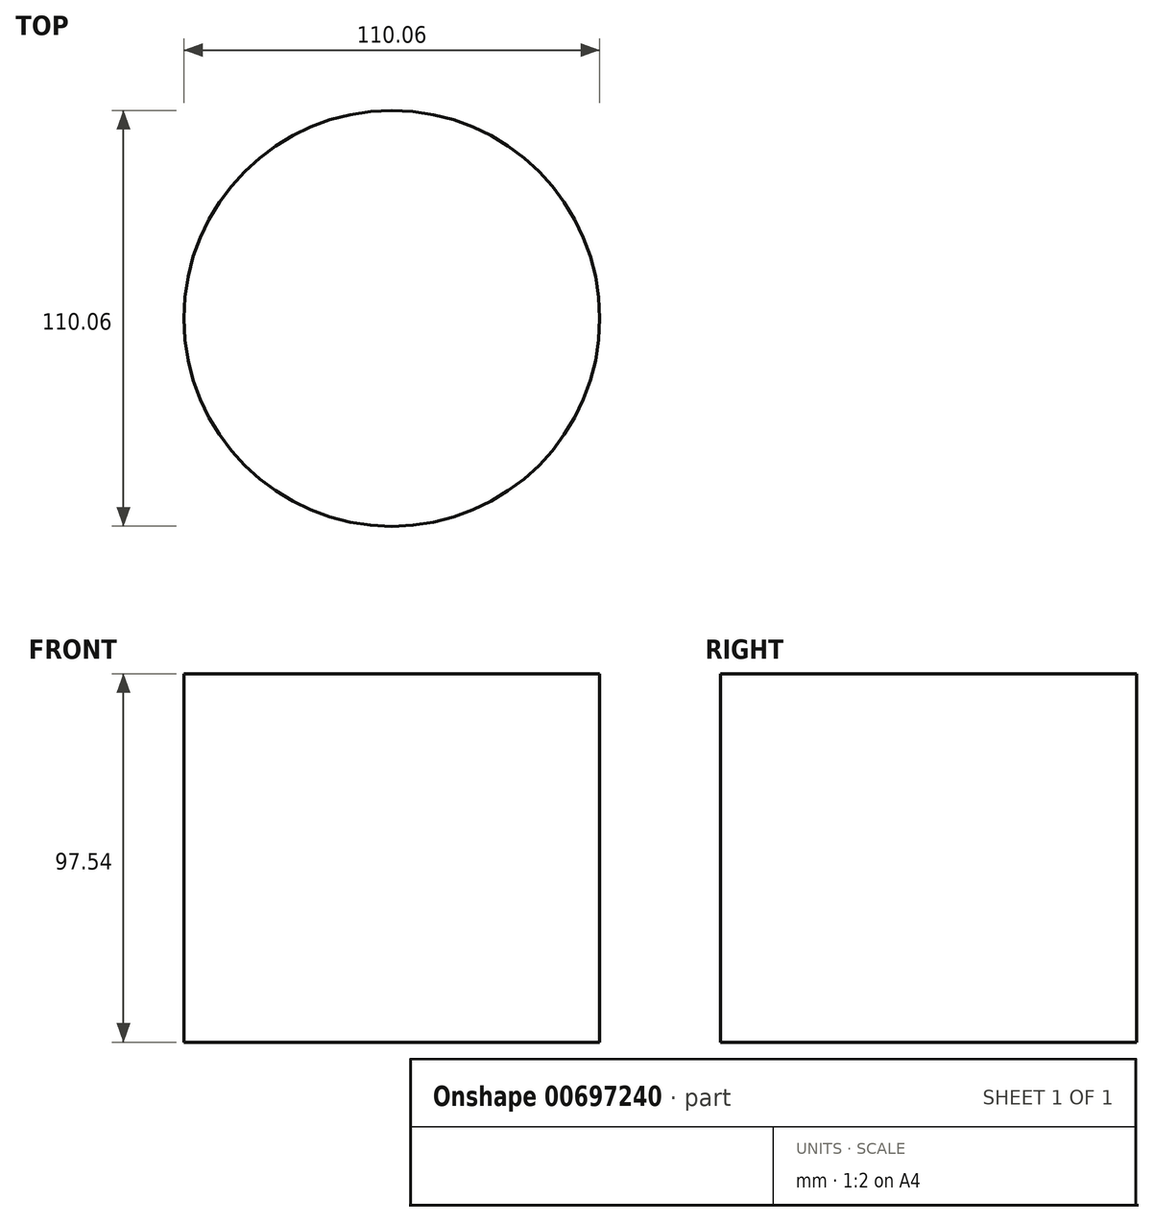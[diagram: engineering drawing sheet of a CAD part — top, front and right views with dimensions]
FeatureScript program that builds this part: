
annotation { "Feature Type Name" : "Feature", "Feature Type Description" : "" }
export const myFeature = defineFeature(function(context is Context, id is Id, definition is map)
    precondition{}
    {
        {
            var Q0;
            Q0=qCreatedBy(makeId("Top.planeOp"),FACE);
            var sketch = newSketch(context, id + "F0", { "sketchPlane" : qUnion([Q0])});
            skCircle(sketch, "E0", {"center": v(5.62, -13.74) * mm, "radius": 55.03 * mm});
            skSolve(sketch);
        }
        {
            var Q0;
            Q0 = qSketchRegion(id + "F0", true);
            extrude(context, id + "F1", {"entities" : qUnion([Q0]), "depth" : 97.54 * mm, "offsetDistance" : 25.4 * mm});
        }
    });
